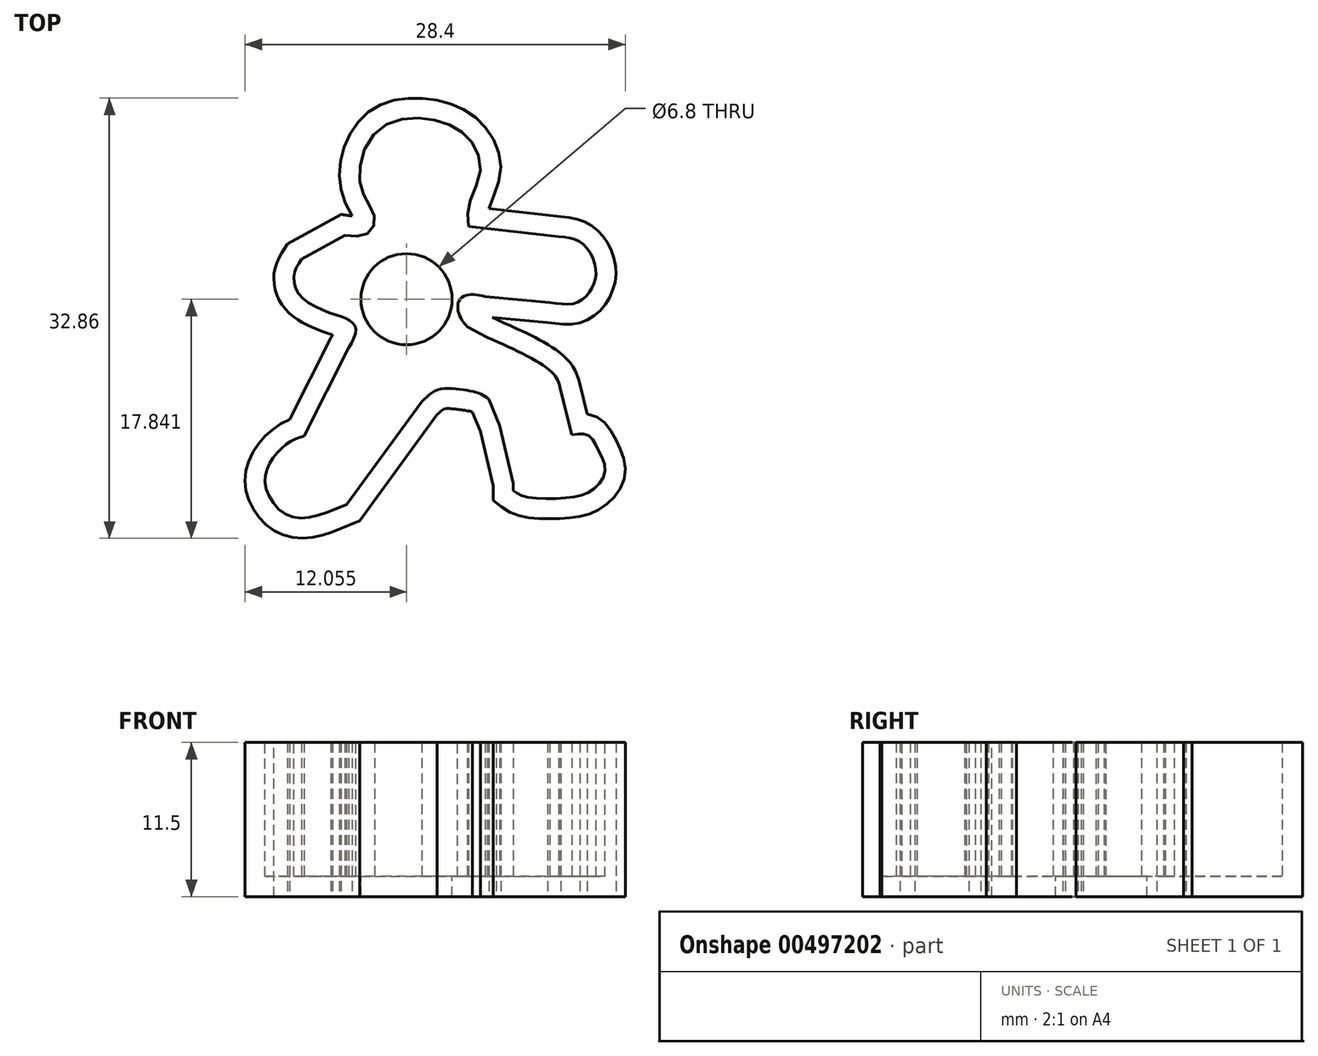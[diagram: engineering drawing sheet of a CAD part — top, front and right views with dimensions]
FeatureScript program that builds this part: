
annotation { "Feature Type Name" : "Feature", "Feature Type Description" : "" }
export const myFeature = defineFeature(function(context is Context, id is Id, definition is map)
    precondition{}
    {
        {
            var Q0;
            Q0=qCreatedBy(makeId("Top.planeOp"),FACE);
            var sketch = newSketch(context, id + "F0", { "sketchPlane" : qUnion([Q0])});
            skLineSegment(sketch, "E0", {"start": v(25.19, -4.55) * mm, "end": v(21.86, -11.15) * mm});
            skLineSegment(sketch, "E1", {"start": v(30.67, -8.58) * mm, "end": v(25.05, -16.26) * mm});
            skLineSegment(sketch, "E2", {"start": v(35.68, -8.42) * mm, "end": v(36.46, -10.35) * mm});
            skLineSegment(sketch, "E3", {"start": v(36.46, -10.35) * mm, "end": v(37.49, -14.69) * mm});
            skLineSegment(sketch, "E4", {"start": v(35.55, -3.79) * mm, "end": v(34.05, -3) * mm});
            skLineSegment(sketch, "E5", {"start": v(41.85, -11.08) * mm, "end": v(41.03, -7.65) * mm});
            skLineSegment(sketch, "E6", {"start": v(34.16, 4.5) * mm, "end": v(40.9, 3.72) * mm});
            skLineSegment(sketch, "E7", {"start": v(35.38, -0.73) * mm, "end": v(40.23, -1.18) * mm});
            skFitSpline(sketch, "E8", {"points": [v(21.68, 2.05) * mm, v(21.12, 0.88) * mm, v(21.68, -0.79) * mm, v(24.3, -2.12) * mm, v(25.41, -2.63) * mm, v(25.75, -3.3) * mm, v(25.19, -4.55) * mm], "startDerivative": vector(-4.7, -6.96) * mm, "endDerivative": vector(-5.19, -8.31) * mm});
            skFitSpline(sketch, "E9", {"points": [v(21.86, -11.15) * mm, v(20.79, -11.6) * mm, v(19.45, -12.93) * mm, v(19, -14.94) * mm, v(20.9, -17.17) * mm, v(25.05, -16.26) * mm], "startDerivative": vector(-7.49, -2.28) * mm, "endDerivative": vector(16.62, 7.16) * mm});
            skFitSpline(sketch, "E10", {"points": [v(35.68, -8.42) * mm, v(35, -7.97) * mm, v(33.71, -7.7) * mm, v(31.87, -7.7) * mm, v(30.67, -8.58) * mm], "startDerivative": vector(-3.19, 2.56) * mm, "endDerivative": vector(-4.09, -4.14) * mm});
            skFitSpline(sketch, "E11", {"points": [v(37.49, -14.69) * mm, v(37.49, -15.22) * mm], "startDerivative": vector(0, -0.53) * mm, "endDerivative": vector(0, -0.53) * mm});
            skFitSpline(sketch, "E12", {"points": [v(37.49, -15.22) * mm, v(38.34, -15.66) * mm, v(41.34, -15.77) * mm, v(43.35, -15.22) * mm, v(44.35, -13.77) * mm, v(43.8, -12.1) * mm, v(43.07, -11.08) * mm, v(41.85, -11.08) * mm], "startDerivative": vector(6.13, -4.68) * mm, "endDerivative": vector(-11.1, -1.97) * mm});
            skFitSpline(sketch, "E13", {"points": [v(24.91, 3.84) * mm, v(26.3, 3.84) * mm, v(27.08, 4.56) * mm, v(26.97, 5.62) * mm, v(26.25, 7.01) * mm, v(26.08, 9.24) * mm, v(27.53, 11.8) * mm, v(30.15, 12.58) * mm, v(32.71, 12.08) * mm, v(34.33, 10.86) * mm, v(35.05, 8.68) * mm, v(34.21, 6.23) * mm, v(34.16, 4.5) * mm], "startDerivative": vector(20.97, -2.95) * mm, "endDerivative": vector(2.2, -21.3) * mm});
            skFitSpline(sketch, "E14", {"points": [v(41.03, -7.65) * mm, v(40.4, -6.41) * mm, v(35.55, -3.79) * mm], "startDerivative": vector(-0.98, 3.66) * mm, "endDerivative": vector(-9.07, 4.02) * mm});
            skFitSpline(sketch, "E15", {"points": [v(34.05, -3) * mm, v(33.55, -2.3) * mm, v(33.38, -1.23) * mm, v(34.05, -0.62) * mm, v(35.38, -0.73) * mm], "startDerivative": vector(-2.4, 2.76) * mm, "endDerivative": vector(4.99, -1.13) * mm});
            skFitSpline(sketch, "E16", {"points": [v(40.23, -1.18) * mm, v(42.3, -1.18) * mm, v(43.4, 0) * mm, v(43.63, 1.5) * mm, v(42.57, 3.28) * mm, v(40.9, 3.72) * mm], "startDerivative": vector(10.42, -1.64) * mm, "endDerivative": vector(-9.05, 0.71) * mm});
            skFitSpline(sketch, "E17", {"points": [v(24.91, 3.84) * mm, v(21.68, 2.05) * mm], "startDerivative": vector(-3.23, -1.78) * mm, "endDerivative": vector(-3.23, -1.78) * mm});
            skSolve(sketch);
        }
        {
            var Q0;
            Q0=makeQuery(id+"F0.imprint","IMPRINT",FACE,{"disambiguationData":[TD([[makeQuery(id+"F0.imprint","IMPRINT",EDGE,{"derivedFrom":sQuery(id+"F0.wireOp",EDGE,"E0")}),1.0]])]});
            extrude(context, id + "F1", {"entities" : qUnion([Q0]), "depth" : 10 * mm});
        }
        {
            var Q0;
            Q0=makeQuery(id+"F1.opExtrude","CAP_FACE",FACE,{"disambiguationData":[OSD([sQuery(id+"F0.wireOp",EDGE,"E0"),sQuery(id+"F0.wireOp",EDGE,"E1"),sQuery(id+"F0.wireOp",EDGE,"E2"),sQuery(id+"F0.wireOp",EDGE,"E3"),sQuery(id+"F0.wireOp",EDGE,"E4"),sQuery(id+"F0.wireOp",EDGE,"E5"),sQuery(id+"F0.wireOp",EDGE,"E6"),sQuery(id+"F0.wireOp",EDGE,"E7"),sQuery(id+"F0.wireOp",EDGE,"E8"),sQuery(id+"F0.wireOp",EDGE,"E9"),sQuery(id+"F0.wireOp",EDGE,"E10"),sQuery(id+"F0.wireOp",EDGE,"E11"),sQuery(id+"F0.wireOp",EDGE,"E12"),sQuery(id+"F0.wireOp",EDGE,"E13"),sQuery(id+"F0.wireOp",EDGE,"E14"),sQuery(id+"F0.wireOp",EDGE,"E15"),sQuery(id+"F0.wireOp",EDGE,"E16"),sQuery(id+"F0.wireOp",EDGE,"E17")])],"isStart":false});
            shell(context, id + "F2", {"entities" : qUnion([Q0]), "thickness" : 1.5 * mm, "oppositeDirection" : true});
        }
        {
            var Q0;
            Q0=qCreatedBy(makeId("Top.planeOp"),FACE);
            var sketch = newSketch(context, id + "F3", { "sketchPlane" : qUnion([Q0])});
            skCircle(sketch, "E18", {"center": v(29.52, -0.94) * mm, "radius": 3.4 * mm});
            skSolve(sketch);
        }
        {
            var Q0;
            Q0=makeQuery(id+"F3.imprint","IMPRINT",FACE,{"disambiguationData":[TD([[makeQuery(id+"F3.imprint","IMPRINT",EDGE,{"derivedFrom":sQuery(id+"F3.wireOp",EDGE,"E18")}),1.0]])]});
            extrude(context, id + "F4", {"entities" : qUnion([Q0]), "operationType" : NewBodyOperationType.REMOVE, "oppositeDirection" : true, "depth" : 25.4 * mm});
        }
    });
